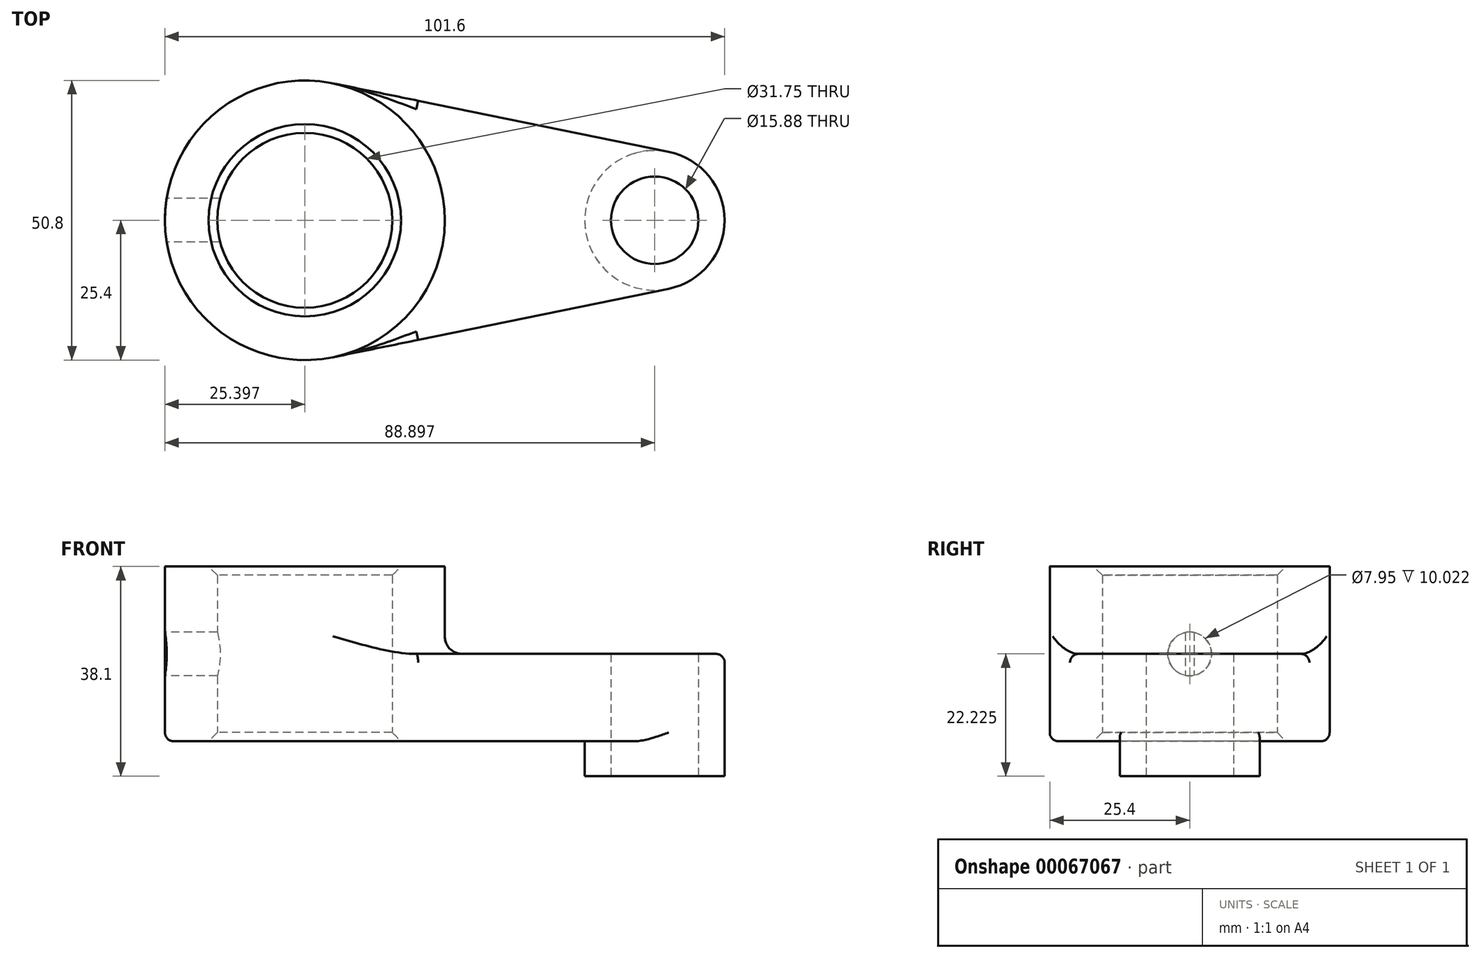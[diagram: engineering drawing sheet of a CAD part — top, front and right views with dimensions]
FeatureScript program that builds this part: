
annotation { "Feature Type Name" : "Feature", "Feature Type Description" : "" }
export const myFeature = defineFeature(function(context is Context, id is Id, definition is map)
    precondition{}
    {
        {
            var Q0;
            Q0=qCreatedBy(makeId("Top.planeOp"),FACE);
            var sketch = newSketch(context, id + "F0", { "sketchPlane" : qUnion([Q0])});
            skCircle(sketch, "E0", {"center": v(-63.51, 0) * mm, "radius": 25.4 * mm});
            skCircle(sketch, "E1", {"center": v(-0.01, 0) * mm, "radius": 12.7 * mm});
            skLineSegment(sketch, "E2", {"start": v(-58.43, 24.89) * mm, "end": v(2.53, 12.44) * mm});
            skLineSegment(sketch, "E3", {"start": v(-58.43, -24.89) * mm, "end": v(2.53, -12.44) * mm});
            skCircle(sketch, "E4", {"center": v(-63.51, 0) * mm, "radius": 15.88 * mm});
            skCircle(sketch, "E5", {"center": v(-0.01, 0) * mm, "radius": 7.94 * mm});
            skSolve(sketch);
        }
        {
            var Q0;
            Q0 = qSketchRegion(id + "F0", true);
            extrude(context, id + "F1", {"entities" : qUnion([Q0]), "depth" : 15.88 * mm});
        }
        {
            var Q0;
            Q0=makeQuery(id+"F0.imprint","IMPRINT",FACE,{"disambiguationData":[TD([[makeQuery(id+"F0.imprint","IMPRINT",EDGE,{"derivedFrom":sQuery(id+"F0.wireOp",EDGE,"E4")}),-1.0]])]});
            extrude(context, id + "F2", {"entities" : qUnion([Q0]), "operationType" : NewBodyOperationType.ADD, "depth" : 31.75 * mm});
        }
        {
            var Q0;
            Q0=makeQuery(id+"F0.imprint","IMPRINT",FACE,{"disambiguationData":[TD([[makeQuery(id+"F0.imprint","IMPRINT",EDGE,{"derivedFrom":sQuery(id+"F0.wireOp",EDGE,"E5")}),-1.0]])]});
            extrude(context, id + "F3", {"entities" : qUnion([Q0]), "operationType" : NewBodyOperationType.ADD, "oppositeDirection" : true, "depth" : 6.35 * mm});
        }
        {
            var Q0;
            Q0=makeQuery(id+"F3.opExtrude","CAP_EDGE",EDGE,{"disambiguationData":[OSD([sQuery(id+"F0.wireOp",EDGE,"E1")])],"isStart":true});
            var Q1;
            {var subQ0=sQuery(id+"F0.wireOp",EDGE,"E0");Q1=makeQuery(id+"F2.boolean.opBoolean","INTERSECT",EDGE,{"derivedFrom":[makeQuery(id+"F1.opExtrude","CAP_FACE",FACE,{"disambiguationData":[OSD([subQ0,sQuery(id+"F0.wireOp",EDGE,"E1"),sQuery(id+"F0.wireOp",EDGE,"E2"),sQuery(id+"F0.wireOp",EDGE,"E3"),sQuery(id+"F0.wireOp",EDGE,"E4"),sQuery(id+"F0.wireOp",EDGE,"E5")])],"isStart":false}),makeQuery(id+"F2.opExtrude","SWEPT_FACE",FACE,{"disambiguationData":[OSD([subQ0])]})]});}
            fillet(context, id + "F4", {"entities" : qUnion([Q0, Q1]), "radius" : 3.17 * mm, "tangentPropagation" : true, "allowEdgeOverflow" : false});
        }
        {
            var Q0;
            Q0=makeQuery(id+"F1.opExtrude","CAP_EDGE",EDGE,{"disambiguationData":[OSD([sQuery(id+"F0.wireOp",EDGE,"E3")])],"isStart":false});
            var Q1;
            Q1=makeQuery(id+"F1.opExtrude","CAP_EDGE",EDGE,{"disambiguationData":[OSD([sQuery(id+"F0.wireOp",EDGE,"E3")])],"isStart":true});
            fillet(context, id + "F5", {"entities" : qUnion([Q0, Q1]), "radius" : 1.59 * mm, "tangentPropagation" : true, "allowEdgeOverflow" : false});
        }
        {
            var Q0;
            Q0=makeQuery(id+"F2.opExtrude","CAP_EDGE",EDGE,{"disambiguationData":[OSD([sQuery(id+"F0.wireOp",EDGE,"E4")])],"isStart":false});
            chamfer(context, id + "F6", {"entities" : qUnion([Q0]), "width" : 1.59 * mm, "tangentPropagation" : true});
        }
        {
            var Q0;
            Q0=makeQuery(id+"F1.opExtrude","CAP_EDGE",EDGE,{"disambiguationData":[OSD([sQuery(id+"F0.wireOp",EDGE,"E4")])],"isStart":true});
            chamfer(context, id + "F7", {"entities" : qUnion([Q0]), "width" : 1.59 * mm, "tangentPropagation" : true});
        }
        {
            var Q0;
            Q0=qCreatedBy(makeId("Right.planeOp"),FACE);
            cPlane(context, id + "F8", {"entities" : qUnion([Q0]), "cplaneType" : CPlaneType.OFFSET, "offset" : 88.9 * mm, "oppositeDirection" : true, "width" : 152.4 * mm, "height" : 152.4 * mm});
        }
        {
            var Q0;
            Q0=qCreatedBy(id+"F8.planeOp",FACE);
            var sketch = newSketch(context, id + "F9", { "sketchPlane" : qUnion([Q0])});
            skCircle(sketch, "E6", {"center": v(0, 15.88) * mm, "radius": 3.98 * mm});
            skSolve(sketch);
        }
        {
            var Q0;
            Q0 = qSketchRegion(id + "F9", true);
            extrude(context, id + "F10", {"entities" : qUnion([Q0]), "operationType" : NewBodyOperationType.REMOVE, "endBound" : BoundingType.UP_TO_NEXT, "depth" : 25.4 * mm});
        }
    });
